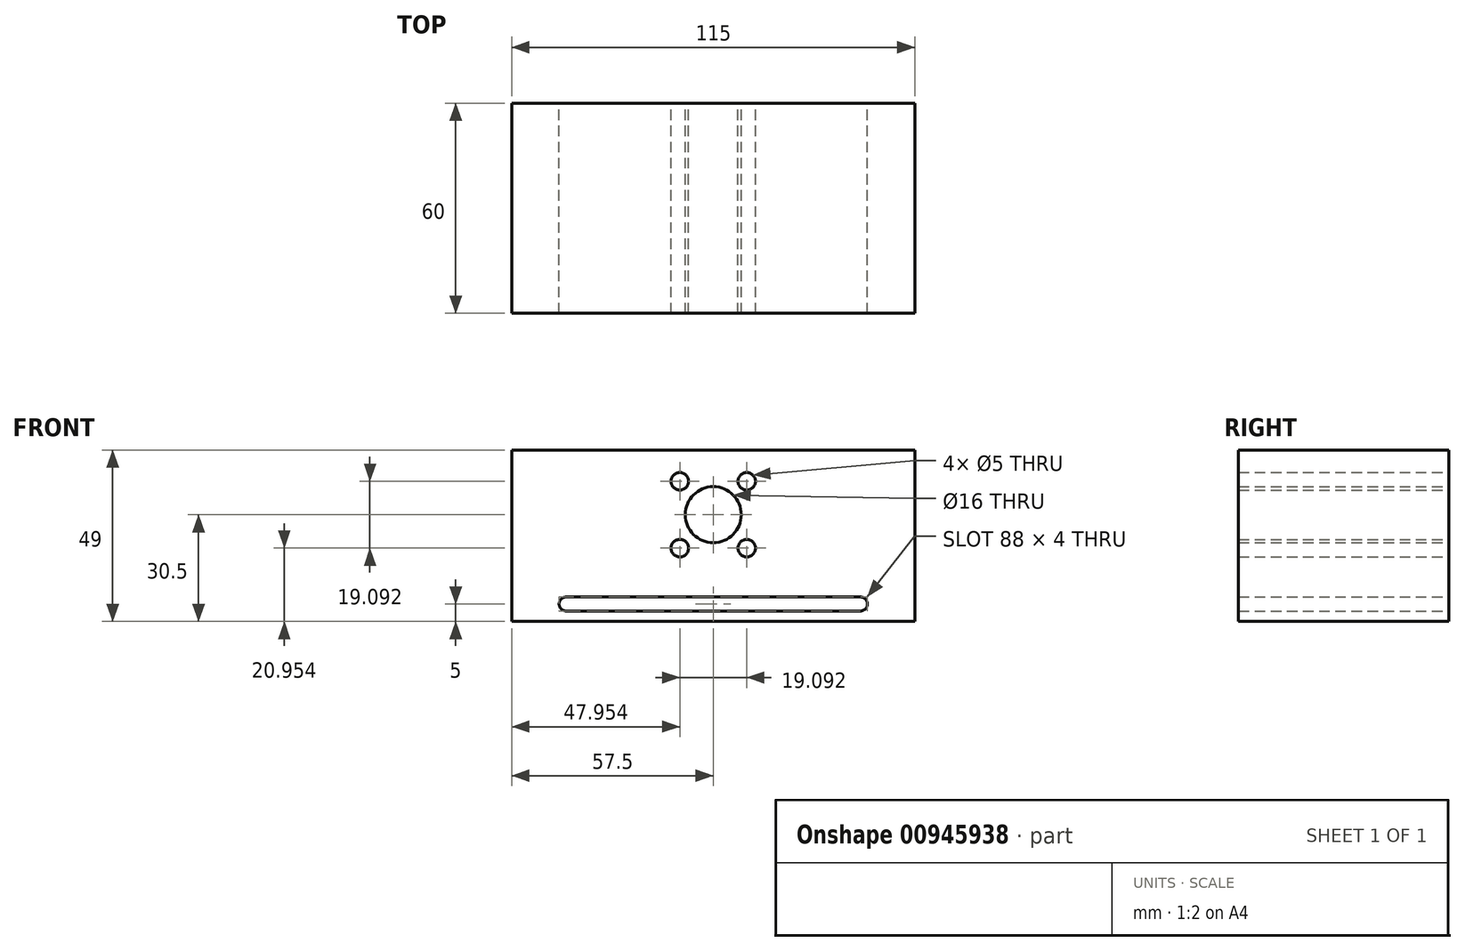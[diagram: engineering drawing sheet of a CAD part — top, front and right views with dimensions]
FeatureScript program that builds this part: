
annotation { "Feature Type Name" : "Feature", "Feature Type Description" : "" }
export const myFeature = defineFeature(function(context is Context, id is Id, definition is map)
    precondition{}
    {
        {
            var Q0;
            Q0=qCreatedBy(makeId("Front.planeOp"),FACE);
            var sketch = newSketch(context, id + "F0", { "sketchPlane" : qUnion([Q0])});
            skLineSegment(sketch, "E0.bottom", {"start": v(57.5, -24.5) * mm, "end": v(-57.5, -24.5) * mm});
            skLineSegment(sketch, "E0.top", {"start": v(57.5, 24.5) * mm, "end": v(-57.5, 24.5) * mm});
            skLineSegment(sketch, "E0.left", {"start": v(57.5, -24.5) * mm, "end": v(57.5, 24.5) * mm});
            skLineSegment(sketch, "E0.right", {"start": v(-57.5, -24.5) * mm, "end": v(-57.5, 24.5) * mm});
            skPoint(sketch, "E0.middle", {"position": v(0, 0) * mm});
            skCircle(sketch, "E1", {"center": v(0, 0) * mm, "radius": 8 * mm, "construction": true});
            skCircle(sketch, "E2", {"center": v(0, 0) * mm, "radius": 13.5 * mm, "construction": true});
            skLineSegment(sketch, "E3.bottom", {"start": v(9.55, 9.55) * mm, "end": v(-9.55, 9.55) * mm, "construction": true});
            skLineSegment(sketch, "E3.top", {"start": v(9.55, -9.55) * mm, "end": v(-9.55, -9.55) * mm, "construction": true});
            skLineSegment(sketch, "E3.left", {"start": v(9.55, 9.55) * mm, "end": v(9.55, -9.55) * mm, "construction": true});
            skLineSegment(sketch, "E3.right", {"start": v(-9.55, 9.55) * mm, "end": v(-9.55, -9.55) * mm, "construction": true});
            skCircle(sketch, "E4", {"center": v(-9.55, 9.55) * mm, "radius": 2.5 * mm, "construction": true});
            skCircle(sketch, "E5", {"center": v(9.55, 9.55) * mm, "radius": 2.5 * mm, "construction": true});
            skCircle(sketch, "E6", {"center": v(9.55, -9.55) * mm, "radius": 2.5 * mm, "construction": true});
            skCircle(sketch, "E7", {"center": v(-9.55, -9.55) * mm, "radius": 2.5 * mm, "construction": true});
            skLineSegment(sketch, "E8.bottom", {"start": v(42, -21.5) * mm, "end": v(-42, -21.5) * mm});
            skLineSegment(sketch, "E8.top", {"start": v(42, -17.5) * mm, "end": v(-42, -17.5) * mm});
            skLineSegment(sketch, "E8.left", {"start": v(44, -19.5) * mm, "end": v(44, -19.5) * mm});
            skLineSegment(sketch, "E8.right", {"start": v(-44, -19.5) * mm, "end": v(-44, -19.5) * mm});
            skPoint(sketch, "E8.middle", {"position": v(0, -19.5) * mm});
            skPoint(sketch, "E9.visualSharp", {"position": v(-44, -21.5) * mm});
            skArc(sketch, "E9.filletArc", {"start": v(-44, -19.5) * mm, "mid": v(-43.41, -20.91) * mm, "end": v(-42, -21.5) * mm});
            skPoint(sketch, "E10.visualSharp", {"position": v(-44, -17.5) * mm});
            skArc(sketch, "E10.filletArc", {"start": v(-42, -17.5) * mm, "mid": v(-43.41, -18.09) * mm, "end": v(-44, -19.5) * mm});
            skPoint(sketch, "E11.visualSharp", {"position": v(44, -17.5) * mm});
            skArc(sketch, "E11.filletArc", {"start": v(44, -19.5) * mm, "mid": v(43.41, -18.09) * mm, "end": v(42, -17.5) * mm});
            skPoint(sketch, "E12.visualSharp", {"position": v(44, -21.5) * mm});
            skArc(sketch, "E12.filletArc", {"start": v(42, -21.5) * mm, "mid": v(43.41, -20.91) * mm, "end": v(44, -19.5) * mm});
            skCircle(sketch, "E13.0.1.0", {"center": v(-9.55, 15.55) * mm, "radius": 2.5 * mm});
            skCircle(sketch, "E13.0.1.1", {"center": v(9.55, 15.55) * mm, "radius": 2.5 * mm});
            skCircle(sketch, "E13.0.1.2", {"center": v(0, 6) * mm, "radius": 8 * mm});
            skCircle(sketch, "E13.0.1.3", {"center": v(-9.55, -3.55) * mm, "radius": 2.5 * mm});
            skCircle(sketch, "E13.0.1.4", {"center": v(9.55, -3.55) * mm, "radius": 2.5 * mm});
            skLineSegment(sketch, "E13.direction1", {"start": v(-9.55, -9.55) * mm, "end": v(15.45, -9.55) * mm, "construction": true});
            skLineSegment(sketch, "E13.direction2", {"start": v(-9.55, -9.55) * mm, "end": v(-9.55, -3.55) * mm, "construction": true});
            skSolve(sketch);
        }
        {
            var Q0;
            Q0 = qSketchRegion(id + "F0", true);
            extrude(context, id + "F1", {"entities" : qUnion([Q0]), "depth" : 60 * mm, "offsetDistance" : 25 * mm});
        }
    });
